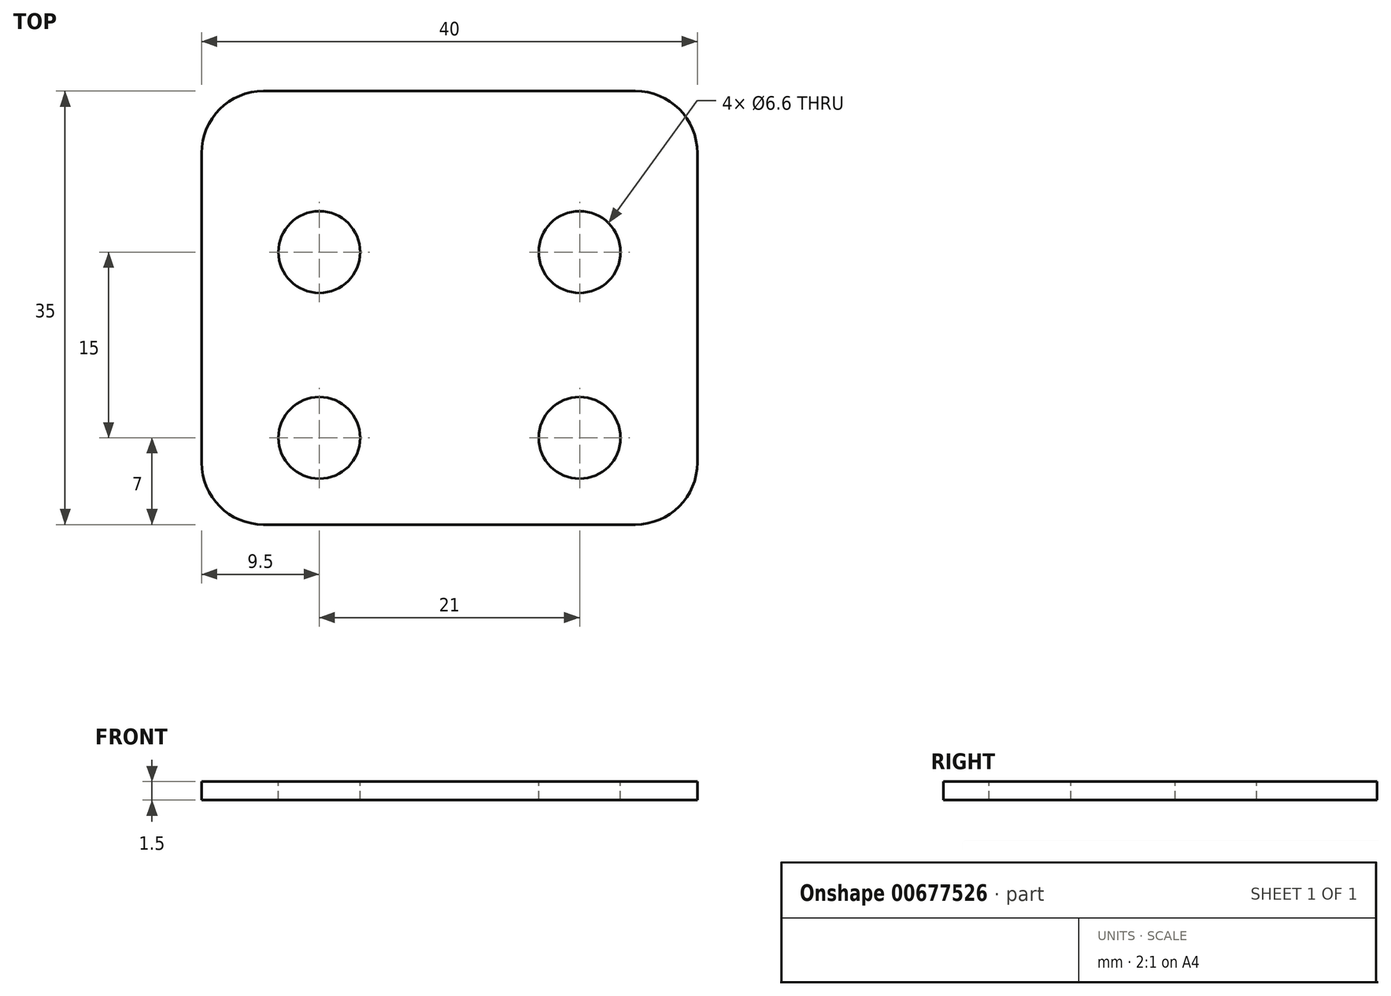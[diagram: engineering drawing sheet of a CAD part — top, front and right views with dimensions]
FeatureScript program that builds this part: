
annotation { "Feature Type Name" : "Feature", "Feature Type Description" : "" }
export const myFeature = defineFeature(function(context is Context, id is Id, definition is map)
    precondition{}
    {
        {
            var Q0;
            Q0=qCreatedBy(makeId("Right.planeOp"),FACE);
            var sketch = newSketch(context, id + "F0", { "sketchPlane" : qUnion([Q0])});
            skLineSegment(sketch, "E0", {"start": v(0, -0.75) * mm, "end": v(35, -0.75) * mm});
            skLineSegment(sketch, "E1", {"start": v(0, 0) * mm, "end": v(0, 60.03) * mm, "construction": true});
            skLineSegment(sketch, "E2", {"start": v(0, 0) * mm, "end": v(0, -0.75) * mm});
            skLineSegment(sketch, "E3.1", {"start": v(0, 0.75) * mm, "end": v(35, 0.75) * mm});
            skLineSegment(sketch, "E4", {"start": v(0, 0.75) * mm, "end": v(0, -0.75) * mm});
            skLineSegment(sketch, "E5", {"start": v(35, -0.75) * mm, "end": v(35, 0.75) * mm});
            skSolve(sketch);
        }
        {
            var Q0;
            Q0=makeQuery(id+"F0.imprint","IMPRINT",FACE,{"disambiguationData":[TD([[makeQuery(id+"F0.imprint","IMPRINT",EDGE,{"derivedFrom":sQuery(id+"F0.wireOp",EDGE,"E0")}),1.0]])]});
            extrude(context, id + "F1", {"entities" : qUnion([Q0]), "depth" : 40 * mm, "offsetDistance" : 25 * mm, "symmetric" : true});
        }
        {
            var Q0;
            Q0=makeQuery(id+"F1.opExtrude","SWEPT_FACE",FACE,{"disambiguationData":[OSD([sQuery(id+"F0.wireOp",EDGE,"E3.1")])]});
            var sketch = newSketch(context, id + "F2", { "sketchPlane" : qUnion([Q0])});
            skPoint(sketch, "E6", {"position": v(-10.5, 7) * mm});
            skPoint(sketch, "E7", {"position": v(-10.5, 22) * mm});
            skPoint(sketch, "E8", {"position": v(10.5, 7) * mm});
            skPoint(sketch, "E9", {"position": v(10.5, 22) * mm});
            skLineSegment(sketch, "E10", {"start": v(-10.5, 7) * mm, "end": v(10.5, 7) * mm, "construction": true});
            skPoint(sketch, "E11", {"position": v(0, 7) * mm});
            skSolve(sketch);
        }
        {
            var Q0;
            Q0=sQuery(id+"F2.wireOp",VERTEX,"E6");
            var Q1;
            Q1=sQuery(id+"F2.wireOp",VERTEX,"E8");
            var Q2;
            Q2=sQuery(id+"F2.wireOp",VERTEX,"E9");
            var Q3;
            Q3=sQuery(id+"F2.wireOp",VERTEX,"E7");
            var Q4;
            Q4=makeQuery(id+"F1.opExtrude","SWEPT_BODY",BODY,{"disambiguationData":[OSD([sQuery(id+"F0.wireOp",EDGE,"E0"),sQuery(id+"F0.wireOp",EDGE,"a3De9Df1-cGyQ-DOXp-Yyzx-AuHUEQyxyMDE"),sQuery(id+"F0.wireOp",EDGE,"E3.0"),sQuery(id+"F0.wireOp",EDGE,"E3.1"),sQuery(id+"F0.wireOp",EDGE,"35m8iNmf-PLOr-8bKS-uMKm-UTE9vmy1P2Um"),sQuery(id+"F0.wireOp",EDGE,"E4")])]});
            hole(context, id + "F3", {"style" : HoleStyle.SIMPLE, "endStyle" : HoleEndStyle.BLIND, "standardTappedOrClearance" : lookupTablePath({ "standard" : "ISO", "fit" : "Normal", "size" : "M6", "type" : "Clearance" }), "standardBlindInLast" : lookupTablePath({ "fit" : "Standard", "standard" : "ISO", "size" : "M6", "type" : "Clearance" }), "holeDiameter" : 6.6 * mm, "majorDiameter" : 6 * mm, "holeDepth" : 43 * mm, "isTappedThrough" : true, "tappedDepth" : 40 * mm, "tapClearance" : 3, "startFromSketch" : true, "locations" : qUnion([Q0, Q1, Q2, Q3]), "scope" : qUnion([Q4])});
        }
        {
            var Q0;
            Q0=makeQuery(id+"F1.opExtrude","CAP_EDGE",EDGE,{"disambiguationData":[OSD([sQuery(id+"F0.wireOp",EDGE,"E4")])],"isStart":false});
            var Q1;
            Q1=makeQuery(id+"F1.opExtrude","CAP_EDGE",EDGE,{"disambiguationData":[OSD([sQuery(id+"F0.wireOp",EDGE,"E4")])],"isStart":true});
            var Q2;
            Q2=makeQuery(id+"F1.opExtrude","CAP_EDGE",EDGE,{"disambiguationData":[OSD([sQuery(id+"F0.wireOp",EDGE,"E5")])],"isStart":false});
            var Q3;
            Q3=makeQuery(id+"F1.opExtrude","CAP_EDGE",EDGE,{"disambiguationData":[OSD([sQuery(id+"F0.wireOp",EDGE,"E5")])],"isStart":true});
            fillet(context, id + "F4", {"entities" : qUnion([Q0, Q1, Q2, Q3]), "radius" : 5 * mm, "tangentPropagation" : true, "allowEdgeOverflow" : false});
        }
    });
